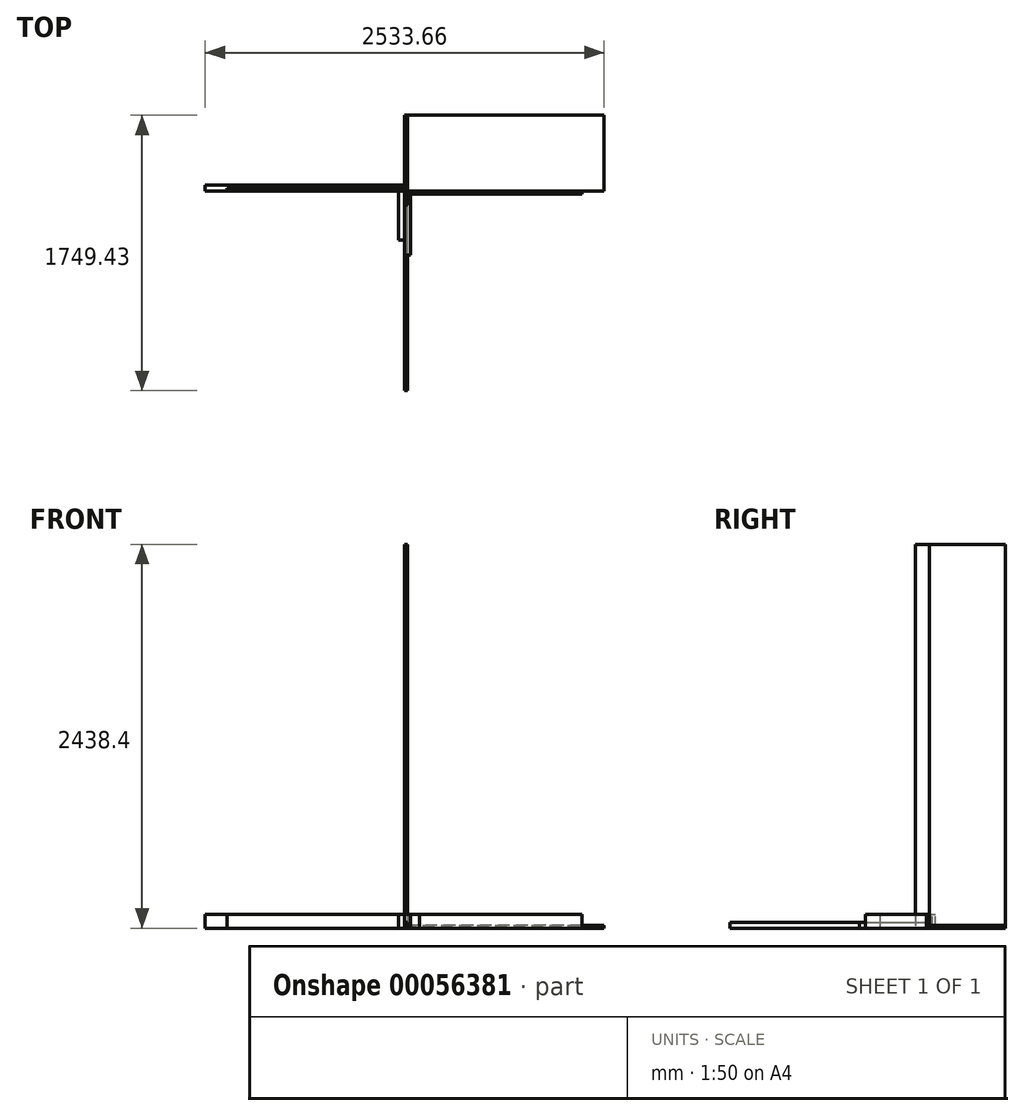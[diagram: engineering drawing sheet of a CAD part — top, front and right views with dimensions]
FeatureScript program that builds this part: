
annotation { "Feature Type Name" : "Feature", "Feature Type Description" : "" }
export const myFeature = defineFeature(function(context is Context, id is Id, definition is map)
    precondition{}
    {
        {
            var Q0;
            Q0=qCreatedBy(makeId("Front.planeOp"),FACE);
            var sketch = newSketch(context, id + "F0", { "sketchPlane" : qUnion([Q0])});
            skLineSegment(sketch, "E0.bottom", {"start": v(0, 0) * mm, "end": v(-38.1, 0) * mm});
            skLineSegment(sketch, "E0.top", {"start": v(0, 88.9) * mm, "end": v(-38.1, 88.9) * mm});
            skLineSegment(sketch, "E0.left", {"start": v(0, 0) * mm, "end": v(0, 88.9) * mm});
            skLineSegment(sketch, "E0.right", {"start": v(-38.1, 0) * mm, "end": v(-38.1, 88.9) * mm});
            skSolve(sketch);
        }
        {
            var Q0;
            Q0 = qSketchRegion(id + "F0", true);
            extrude(context, id + "F1", {"entities" : qUnion([Q0]), "depth" : 311.15 * mm});
        }
        {
            var Q0;
            Q0=qCreatedBy(makeId("Right.planeOp"),FACE);
            var sketch = newSketch(context, id + "F2", { "sketchPlane" : qUnion([Q0])});
            skLineSegment(sketch, "E1.bottom", {"start": v(0, 0) * mm, "end": v(38.1, 0) * mm});
            skLineSegment(sketch, "E1.top", {"start": v(0, 88.9) * mm, "end": v(38.1, 88.9) * mm});
            skLineSegment(sketch, "E1.left", {"start": v(0, 0) * mm, "end": v(0, 88.9) * mm});
            skLineSegment(sketch, "E1.right", {"start": v(38.1, 0) * mm, "end": v(38.1, 88.9) * mm});
            skSolve(sketch);
        }
        {
            var Q0;
            Q0=makeQuery(id+"F2.imprint","IMPRINT",FACE,{"disambiguationData":[TD([[makeQuery(id+"F2.imprint","IMPRINT",EDGE,{"derivedFrom":sQuery(id+"F2.wireOp",EDGE,"E1.bottom")}),1.0]])]});
            extrude(context, id + "F3", {"entities" : qUnion([Q0]), "oppositeDirection" : true, "depth" : 1266.82 * mm});
        }
        {
            var Q0;
            Q0=qCreatedBy(makeId("Right.planeOp"),FACE);
            var sketch = newSketch(context, id + "F4", { "sketchPlane" : qUnion([Q0])});
            skLineSegment(sketch, "E2.bottom", {"start": v(0, 0) * mm, "end": v(482.6, 0) * mm});
            skLineSegment(sketch, "E2.top", {"start": v(0, 2438.4) * mm, "end": v(482.6, 2438.4) * mm});
            skLineSegment(sketch, "E2.left", {"start": v(0, 0) * mm, "end": v(0, 2438.4) * mm});
            skLineSegment(sketch, "E2.right", {"start": v(482.6, 0) * mm, "end": v(482.6, 2438.4) * mm});
            skSolve(sketch);
        }
        {
            var Q0;
            Q0 = qSketchRegion(id + "F4", true);
            extrude(context, id + "F5", {"entities" : qUnion([Q0]), "depth" : 19.05 * mm});
        }
        {
            var Q0;
            Q0=qCreatedBy(makeId("Front.planeOp"),FACE);
            var sketch = newSketch(context, id + "F6", { "sketchPlane" : qUnion([Q0])});
            skLineSegment(sketch, "E3.bottom", {"start": v(0, 0) * mm, "end": v(38.1, 0) * mm});
            skLineSegment(sketch, "E3.top", {"start": v(0, 88.9) * mm, "end": v(38.1, 88.9) * mm});
            skLineSegment(sketch, "E3.left", {"start": v(0, 0) * mm, "end": v(0, 88.9) * mm});
            skLineSegment(sketch, "E3.right", {"start": v(38.1, 0) * mm, "end": v(38.1, 88.9) * mm});
            skSolve(sketch);
        }
        {
            var Q0;
            Q0=makeQuery(id+"F6.imprint","IMPRINT",FACE,{"disambiguationData":[TD([[makeQuery(id+"F6.imprint","IMPRINT",EDGE,{"derivedFrom":sQuery(id+"F6.wireOp",EDGE,"E3.bottom")}),1.0]])]});
            extrude(context, id + "F7", {"entities" : qUnion([Q0]), "depth" : 406.4 * mm});
        }
        {
            var Q0;
            Q0=qCreatedBy(makeId("Right.planeOp"),FACE);
            var sketch = newSketch(context, id + "F8", { "sketchPlane" : qUnion([Q0])});
            skLineSegment(sketch, "E4.bottom", {"start": v(0, 0) * mm, "end": v(19.05, 0) * mm});
            skLineSegment(sketch, "E4.top", {"start": v(0, 88.9) * mm, "end": v(19.05, 88.9) * mm});
            skLineSegment(sketch, "E4.left", {"start": v(0, 0) * mm, "end": v(0, 88.9) * mm});
            skLineSegment(sketch, "E4.right", {"start": v(19.05, 0) * mm, "end": v(19.05, 88.9) * mm});
            skSolve(sketch);
        }
        {
            var Q0;
            Q0=makeQuery(id+"F8.imprint","IMPRINT",FACE,{"disambiguationData":[TD([[makeQuery(id+"F8.imprint","IMPRINT",EDGE,{"derivedFrom":sQuery(id+"F8.wireOp",EDGE,"E4.bottom")}),1.0]])]});
            extrude(context, id + "F9", {"entities" : qUnion([Q0]), "oppositeDirection" : true, "depth" : 1127.12 * mm});
        }
        {
            var Q0;
            Q0=qCreatedBy(makeId("Top.planeOp"),FACE);
            var sketch = newSketch(context, id + "F10", { "sketchPlane" : qUnion([Q0])});
            skLineSegment(sketch, "E5.bottom", {"start": v(0, 0) * mm, "end": v(19.05, 0) * mm});
            skLineSegment(sketch, "E5.top", {"start": v(0, -88.9) * mm, "end": v(19.05, -88.9) * mm});
            skLineSegment(sketch, "E5.left", {"start": v(0, 0) * mm, "end": v(0, -88.9) * mm});
            skLineSegment(sketch, "E5.right", {"start": v(19.05, 0) * mm, "end": v(19.05, -88.9) * mm});
            skSolve(sketch);
        }
        {
            var Q0;
            Q0=makeQuery(id+"F10.imprint","IMPRINT",FACE,{"disambiguationData":[TD([[makeQuery(id+"F10.imprint","IMPRINT",EDGE,{"derivedFrom":sQuery(id+"F10.wireOp",EDGE,"E5.bottom")}),-1.0]])]});
            extrude(context, id + "F11", {"entities" : qUnion([Q0]), "depth" : 2438.4 * mm});
        }
        {
            var Q0;
            Q0=qCreatedBy(makeId("Front.planeOp"),FACE);
            var sketch = newSketch(context, id + "F12", { "sketchPlane" : qUnion([Q0])});
            skLineSegment(sketch, "E6.bottom", {"start": v(0, 0) * mm, "end": v(95.25, 0) * mm});
            skLineSegment(sketch, "E6.top", {"start": v(0, 88.9) * mm, "end": v(95.25, 88.9) * mm});
            skLineSegment(sketch, "E6.left", {"start": v(0, 0) * mm, "end": v(0, 88.9) * mm});
            skLineSegment(sketch, "E6.right", {"start": v(95.25, 0) * mm, "end": v(95.25, 88.9) * mm});
            skSolve(sketch);
        }
        {
            var Q0;
            Q0=makeQuery(id+"F12.imprint","IMPRINT",FACE,{"disambiguationData":[TD([[makeQuery(id+"F12.imprint","IMPRINT",EDGE,{"derivedFrom":sQuery(id+"F12.wireOp",EDGE,"E6.bottom")}),1.0]])]});
            extrude(context, id + "F13", {"entities" : qUnion([Q0]), "depth" : 19.05 * mm});
        }
        {
            var Q0;
            Q0=qCreatedBy(makeId("Front.planeOp"),FACE);
            var sketch = newSketch(context, id + "F14", { "sketchPlane" : qUnion([Q0])});
            skLineSegment(sketch, "E7.bottom", {"start": v(0, 0) * mm, "end": v(1127.13, 0) * mm});
            skLineSegment(sketch, "E7.top", {"start": v(0, 88.9) * mm, "end": v(1127.13, 88.9) * mm});
            skLineSegment(sketch, "E7.left", {"start": v(0, 0) * mm, "end": v(0, 88.9) * mm});
            skLineSegment(sketch, "E7.right", {"start": v(1127.13, 0) * mm, "end": v(1127.13, 88.9) * mm});
            skSolve(sketch);
        }
        {
            var Q0;
            Q0=makeQuery(id+"F14.imprint","IMPRINT",FACE,{"disambiguationData":[TD([[makeQuery(id+"F14.imprint","IMPRINT",EDGE,{"derivedFrom":sQuery(id+"F14.wireOp",EDGE,"E7.bottom")}),1.0]])]});
            extrude(context, id + "F15", {"entities" : qUnion([Q0]), "depth" : 19.05 * mm});
        }
        {
            var Q0;
            Q0=qCreatedBy(makeId("Top.planeOp"),FACE);
            var sketch = newSketch(context, id + "F16", { "sketchPlane" : qUnion([Q0])});
            skLineSegment(sketch, "E8", {"start": v(0, 0) * mm, "end": v(0, 482.6) * mm});
            skLineSegment(sketch, "E9", {"start": v(0, 482.6) * mm, "end": v(1266.83, 482.6) * mm});
            skLineSegment(sketch, "E10", {"start": v(1266.83, 482.6) * mm, "end": v(1266.83, 0) * mm});
            skLineSegment(sketch, "E11", {"start": v(1266.83, 0) * mm, "end": v(0, 0) * mm});
            skSolve(sketch);
        }
        {
            var Q0;
            Q0=makeQuery(id+"F16.imprint","IMPRINT",FACE,{"disambiguationData":[TD([[makeQuery(id+"F16.imprint","IMPRINT",EDGE,{"derivedFrom":sQuery(id+"F16.wireOp",EDGE,"E8")}),-1.0]])]});
            extrude(context, id + "F17", {"entities" : qUnion([Q0]), "depth" : 19.05 * mm});
        }
        {
            var Q0;
            Q0=qCreatedBy(makeId("Front.planeOp"),FACE);
            var sketch = newSketch(context, id + "F18", { "sketchPlane" : qUnion([Q0])});
            skLineSegment(sketch, "E12.bottom", {"start": v(0, 0) * mm, "end": v(19.05, 0) * mm});
            skLineSegment(sketch, "E12.top", {"start": v(0, 38.1) * mm, "end": v(19.05, 38.1) * mm});
            skLineSegment(sketch, "E12.left", {"start": v(0, 0) * mm, "end": v(0, 38.1) * mm});
            skLineSegment(sketch, "E12.right", {"start": v(19.05, 0) * mm, "end": v(19.05, 38.1) * mm});
            skSolve(sketch);
        }
        {
            var Q0;
            Q0=makeQuery(id+"F18.imprint","IMPRINT",FACE,{"disambiguationData":[TD([[makeQuery(id+"F18.imprint","IMPRINT",EDGE,{"derivedFrom":sQuery(id+"F18.wireOp",EDGE,"E12.bottom")}),1.0]])]});
            extrude(context, id + "F19", {"entities" : qUnion([Q0]), "depth" : 444.5 * mm});
        }
        {
            var Q0;
            Q0=qCreatedBy(makeId("Front.planeOp"),FACE);
            var sketch = newSketch(context, id + "F20", { "sketchPlane" : qUnion([Q0])});
            skLineSegment(sketch, "E13.bottom", {"start": v(0, 0) * mm, "end": v(19.05, 0) * mm});
            skLineSegment(sketch, "E13.top", {"start": v(0, 38.1) * mm, "end": v(19.05, 38.1) * mm});
            skLineSegment(sketch, "E13.left", {"start": v(0, 0) * mm, "end": v(0, 38.1) * mm});
            skLineSegment(sketch, "E13.right", {"start": v(19.05, 0) * mm, "end": v(19.05, 38.1) * mm});
            skSolve(sketch);
        }
        {
            var Q0;
            Q0 = qSketchRegion(id + "F20", true);
            extrude(context, id + "F21", {"entities" : qUnion([Q0]), "depth" : 1266.82 * mm});
        }
    });
